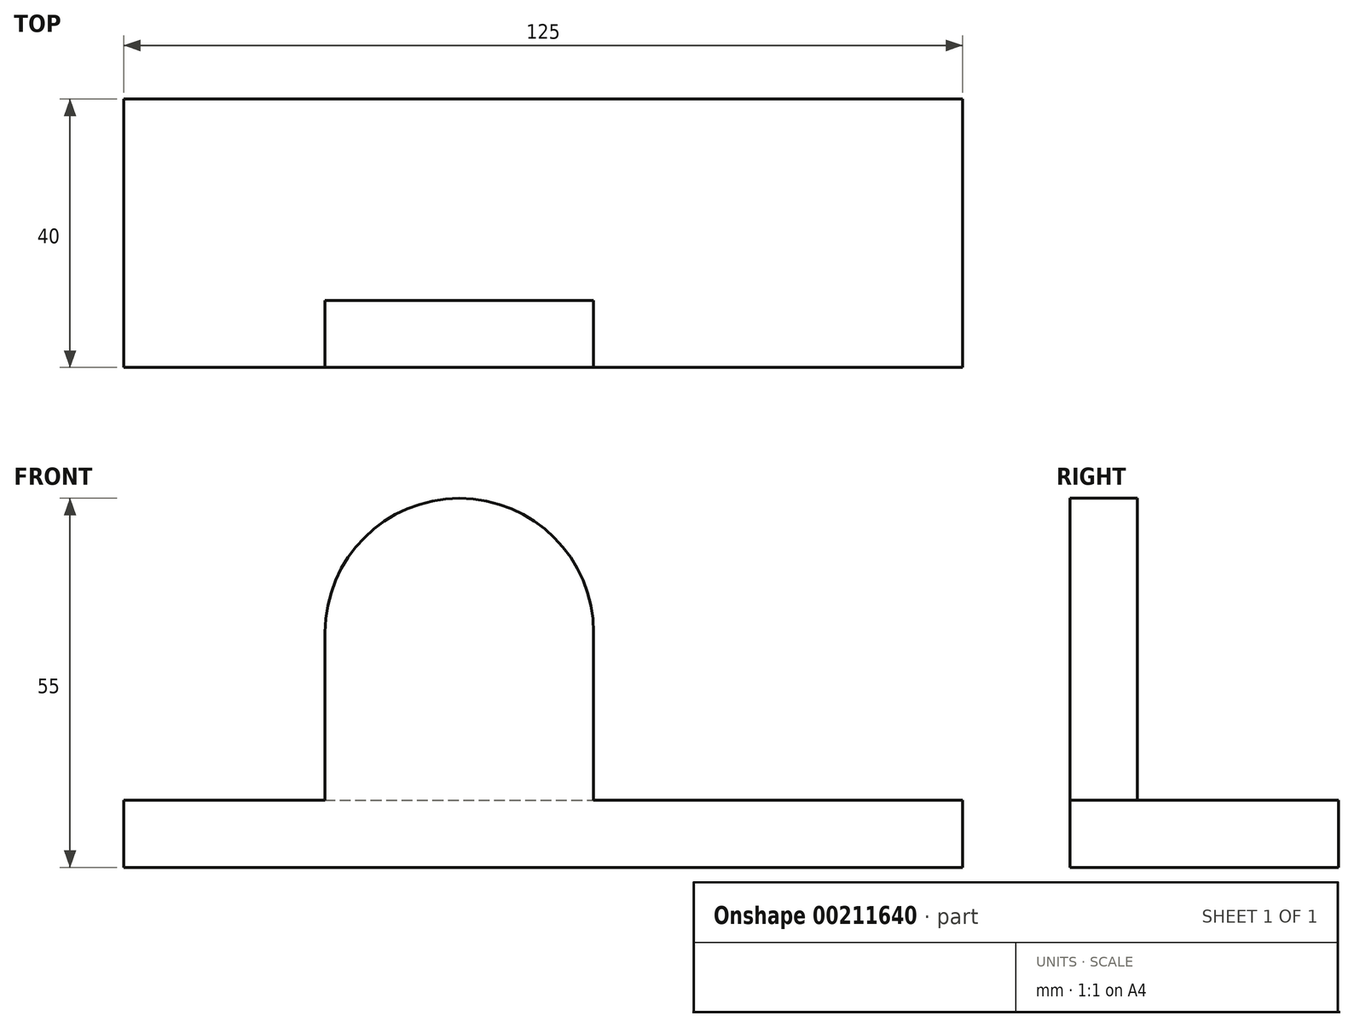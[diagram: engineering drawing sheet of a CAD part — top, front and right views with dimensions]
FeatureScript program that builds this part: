
annotation { "Feature Type Name" : "Feature", "Feature Type Description" : "" }
export const myFeature = defineFeature(function(context is Context, id is Id, definition is map)
    precondition{}
    {
        {
            var Q0;
            Q0=qCreatedBy(makeId("Top.planeOp"),FACE);
            var sketch = newSketch(context, id + "F0", { "sketchPlane" : qUnion([Q0])});
            skLineSegment(sketch, "E0.bottom", {"start": v(0, 0) * mm, "end": v(125, 0) * mm});
            skLineSegment(sketch, "E0.top", {"start": v(0, 40) * mm, "end": v(125, 40) * mm});
            skLineSegment(sketch, "E0.left", {"start": v(0, 0) * mm, "end": v(0, 40) * mm});
            skLineSegment(sketch, "E0.right", {"start": v(125, 0) * mm, "end": v(125, 40) * mm});
            skSolve(sketch);
        }
        {
            var Q0;
            Q0 = qSketchRegion(id + "F0", true);
            extrude(context, id + "F1", {"entities" : qUnion([Q0]), "depth" : 10 * mm});
        }
        {
            var Q0;
            Q0=makeQuery(id+"F1.opExtrude","SWEPT_FACE",FACE,{"disambiguationData":[OSD([sQuery(id+"F0.wireOp",EDGE,"E0.bottom")])]});
            var sketch = newSketch(context, id + "F2", { "sketchPlane" : qUnion([Q0])});
            skLineSegment(sketch, "E1", {"start": v(30, 0) * mm, "end": v(30, 35) * mm});
            skArc(sketch, "E2", {"start": v(30, 35) * mm, "mid": v(50, 55) * mm, "end": v(70, 35) * mm});
            skLineSegment(sketch, "E3", {"start": v(70, 35) * mm, "end": v(70, 0) * mm});
            skLineSegment(sketch, "E4", {"start": v(70, 0) * mm, "end": v(30, 0) * mm});
            skSolve(sketch);
        }
        {
            var Q0;
            Q0 = qSketchRegion(id + "F2", true);
            extrude(context, id + "F3", {"entities" : qUnion([Q0]), "operationType" : NewBodyOperationType.ADD, "oppositeDirection" : true, "depth" : 10 * mm});
        }
    });
